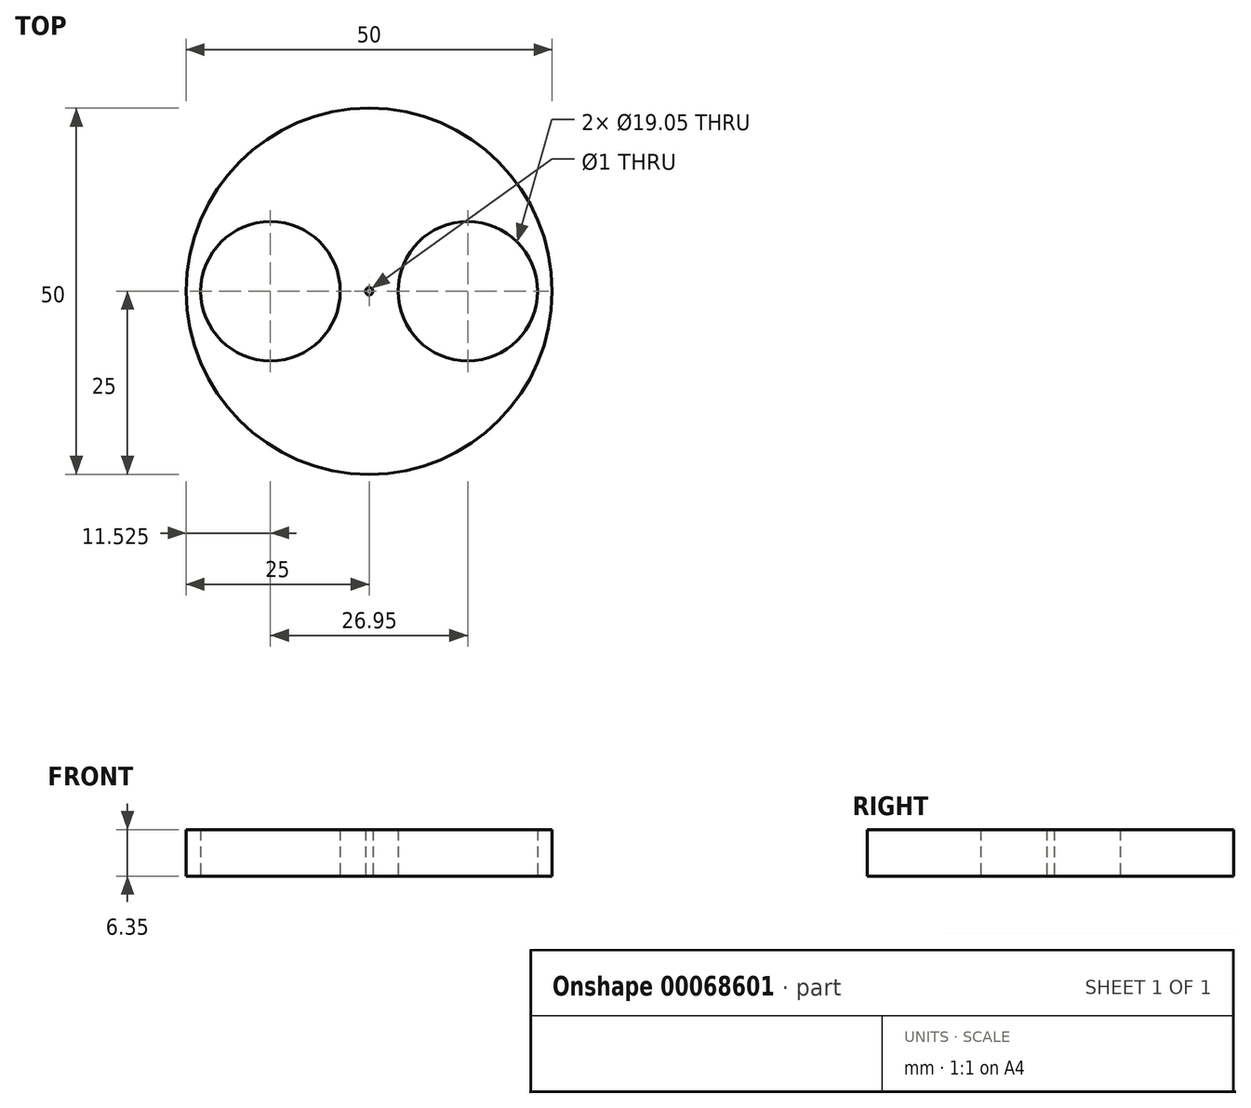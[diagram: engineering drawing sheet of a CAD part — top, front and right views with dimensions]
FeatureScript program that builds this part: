
annotation { "Feature Type Name" : "Feature", "Feature Type Description" : "" }
export const myFeature = defineFeature(function(context is Context, id is Id, definition is map)
    precondition{}
    {
        {
            var Q0;
            Q0=qCreatedBy(makeId("Top.planeOp"),FACE);
            var sketch = newSketch(context, id + "F0", { "sketchPlane" : qUnion([Q0])});
            skCircle(sketch, "E0", {"center": v(0, 0) * mm, "radius": 25 * mm});
            skCircle(sketch, "E1", {"center": v(-13.47, 0) * mm, "radius": 9.53 * mm});
            skCircle(sketch, "E2", {"center": v(13.48, 0) * mm, "radius": 9.53 * mm});
            skCircle(sketch, "E3", {"center": v(0, 0) * mm, "radius": 0.5 * mm});
            skSolve(sketch);
        }
        {
            var Q0;
            Q0 = qSketchRegion(id + "F0", true);
            extrude(context, id + "F1", {"entities" : qUnion([Q0]), "depth" : 6.35 * mm});
        }
    });
